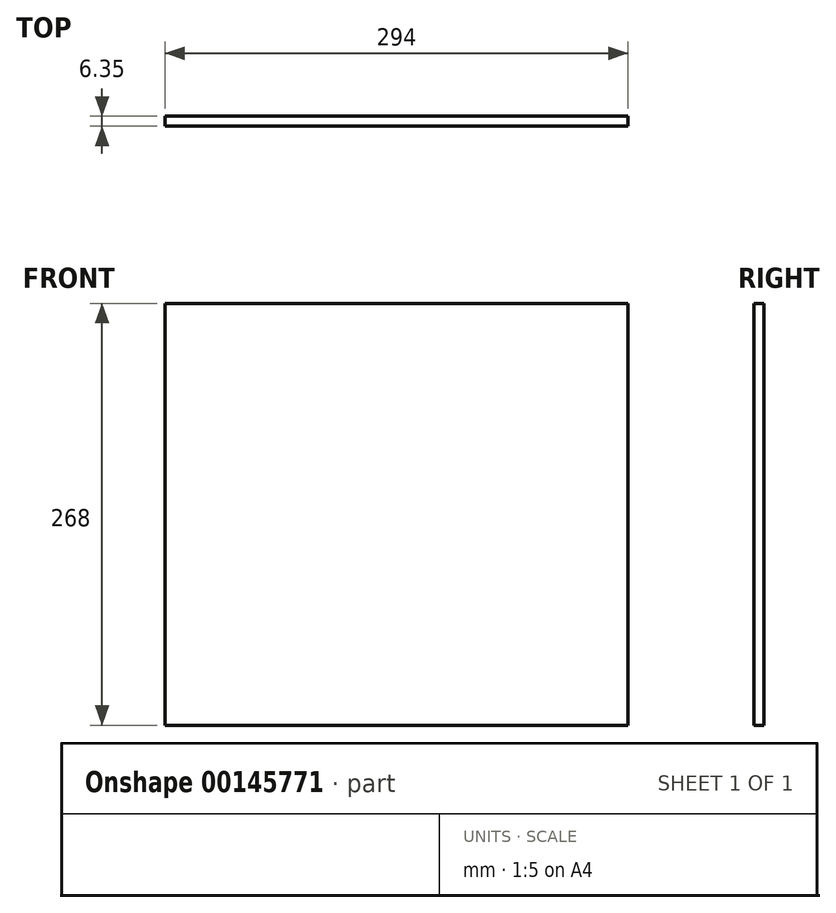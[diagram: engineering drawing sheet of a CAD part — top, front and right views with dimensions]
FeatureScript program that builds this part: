
annotation { "Feature Type Name" : "Feature", "Feature Type Description" : "" }
export const myFeature = defineFeature(function(context is Context, id is Id, definition is map)
    precondition{}
    {
        {
            var Q0;
            Q0=qCreatedBy(makeId("Front.planeOp"),FACE);
            var sketch = newSketch(context, id + "F0", { "sketchPlane" : qUnion([Q0])});
            skLineSegment(sketch, "E0.bottom", {"start": v(-147.72, 127.6) * mm, "end": v(146.28, 127.6) * mm});
            skLineSegment(sketch, "E0.top", {"start": v(-147.72, -140.4) * mm, "end": v(146.28, -140.4) * mm});
            skLineSegment(sketch, "E0.left", {"start": v(-147.72, 127.6) * mm, "end": v(-147.72, -140.4) * mm});
            skLineSegment(sketch, "E0.right", {"start": v(146.28, 127.6) * mm, "end": v(146.28, -140.4) * mm});
            skSolve(sketch);
        }
        {
            var Q0;
            Q0=makeQuery(id+"F0.imprint","IMPRINT",FACE,{"disambiguationData":[TD([[makeQuery(id+"F0.imprint","IMPRINT",EDGE,{"derivedFrom":sQuery(id+"F0.wireOp",EDGE,"E0.bottom")}),-1.0]])]});
            extrude(context, id + "F1", {"entities" : qUnion([Q0]), "depth" : 6.35 * mm});
        }
    });
